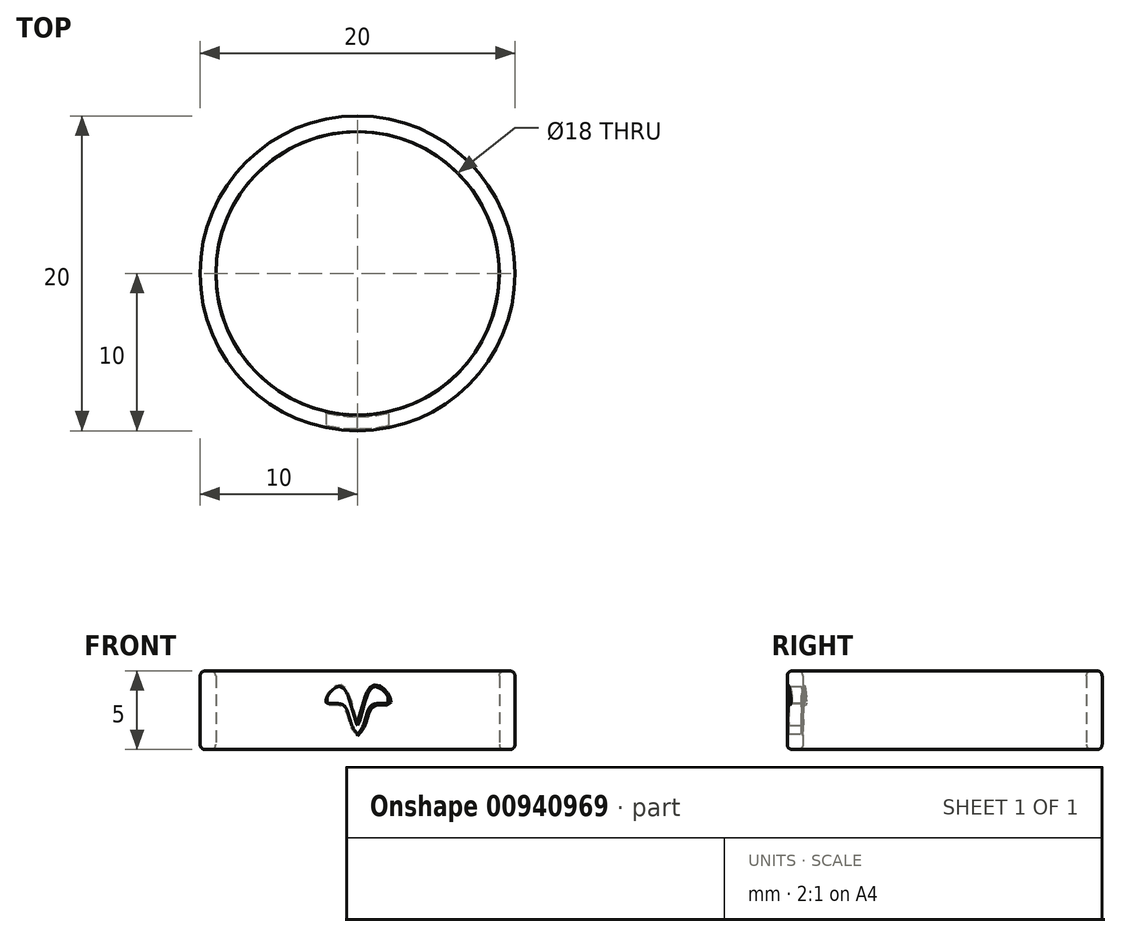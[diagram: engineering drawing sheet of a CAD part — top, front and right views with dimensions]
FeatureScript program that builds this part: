
annotation { "Feature Type Name" : "Feature", "Feature Type Description" : "" }
export const myFeature = defineFeature(function(context is Context, id is Id, definition is map)
    precondition{}
    {
        {
            var Q0;
            Q0=qCreatedBy(makeId("Front.planeOp"),FACE);
            var sketch = newSketch(context, id + "F0", { "sketchPlane" : qUnion([Q0])});
            skLineSegment(sketch, "E0", {"start": v(0, 0) * mm, "end": v(0, 2.47) * mm, "construction": true});
            skLineSegment(sketch, "E1.bottom", {"start": v(9, 0) * mm, "end": v(10, 0) * mm});
            skLineSegment(sketch, "E1.top", {"start": v(9, 5) * mm, "end": v(10, 5) * mm});
            skLineSegment(sketch, "E1.left", {"start": v(9, 0) * mm, "end": v(9, 5) * mm});
            skLineSegment(sketch, "E1.right", {"start": v(10, 0) * mm, "end": v(10, 5) * mm});
            skSolve(sketch);
        }
        {
            var Q0;
            Q0=makeQuery(id+"F0.imprint","IMPRINT",FACE,{"disambiguationData":[TD([[makeQuery(id+"F0.imprint","IMPRINT",EDGE,{"derivedFrom":sQuery(id+"F0.wireOp",EDGE,"E1.bottom")}),1.0]])]});
            var Q1;
            Q1=sQuery(id+"F0.wireOp",EDGE,"E0");
            revolve(context, id + "F1", {"surfaceOperationType" : NewSurfaceOperationType.NEW, "entities" : qUnion([Q0]), "axis" : qUnion([Q1]), "revolveType" : RevolveType.FULL});
        }
        {
            var Q0;
            Q0=makeQuery(id+"F1.opRevolve","SWEPT_EDGE",EDGE,{"disambiguationData":[OSD([sQuery(id+"F0.wireOp",EDGE,"E1.bottom"),sQuery(id+"F0.wireOp",EDGE,"E1.left")])]});
            var Q1;
            Q1=makeQuery(id+"F1.opRevolve","SWEPT_EDGE",EDGE,{"disambiguationData":[OSD([sQuery(id+"F0.wireOp",EDGE,"E1.top"),sQuery(id+"F0.wireOp",EDGE,"E1.left")])]});
            var Q2;
            Q2=makeQuery(id+"F1.opRevolve","SWEPT_EDGE",EDGE,{"disambiguationData":[OSD([sQuery(id+"F0.wireOp",EDGE,"E1.top"),sQuery(id+"F0.wireOp",EDGE,"E1.right")])]});
            var Q3;
            Q3=makeQuery(id+"F1.opRevolve","SWEPT_EDGE",EDGE,{"disambiguationData":[OSD([sQuery(id+"F0.wireOp",EDGE,"E1.bottom"),sQuery(id+"F0.wireOp",EDGE,"E1.right")])]});
            fillet(context, id + "F2", {"entities" : qUnion([Q0, Q1, Q2, Q3]), "radius" : .33 * mm, "tangentPropagation" : true, "allowEdgeOverflow" : false});
        }
        {
            var Q0;
            Q0=qCreatedBy(makeId("Front.planeOp"),FACE);
            var sketch = newSketch(context, id + "F3", { "sketchPlane" : qUnion([Q0])});
            skLineSegment(sketch, "E2", {"start": v(0, 0) * mm, "end": v(0, 7.67) * mm, "construction": true});
            skLineSegment(sketch, "E3", {"start": v(0, 4) * mm, "end": v(3.23, 4) * mm, "construction": true});
            skLineSegment(sketch, "E4", {"start": v(0, 1) * mm, "end": v(2.17, 1) * mm, "construction": true});
            skLineSegment(sketch, "E5", {"start": v(2, 5.06) * mm, "end": v(2, 0.26) * mm, "construction": true});
            skFitSpline(sketch, "E6", {"points": [v(0, 1.55) * mm, v(1.08, 4) * mm, v(2, 3.03) * mm, v(0.94, 2.85) * mm, v(0, 1) * mm], "startDerivative": vector(2.7, 3.62) * mm, "endDerivative": vector(-6.5, -5.91) * mm});
            skFitSpline(sketch, "E7.MirrorCS", {"points": [v(0, 1.55) * mm, v(-1.08, 4) * mm, v(-2, 3.03) * mm, v(-0.94, 2.85) * mm, v(0, 1) * mm], "startDerivative": vector(-2.7, 3.62) * mm, "endDerivative": vector(6.5, -5.91) * mm});
            skSolve(sketch);
        }
        {
            var Q0;
            Q0=makeQuery(id+"F3.imprint","IMPRINT",FACE,{"disambiguationData":[TD([[makeQuery(id+"F3.imprint","IMPRINT",EDGE,{"derivedFrom":sQuery(id+"F3.wireOp",EDGE,"E6")}),-1.0]])]});
            extrude(context, id + "F4", {"entities" : qUnion([Q0]), "operationType" : NewBodyOperationType.REMOVE, "endBound" : BoundingType.THROUGH_ALL, "depth" : 25 * mm, "offsetDistance" : 25 * mm});
        }
        {
            var Q0;
            Q0=makeQuery(id+"F4.boolean.opBoolean","INTERSECT",EDGE,{"derivedFrom":[makeQuery(id+"F1.opRevolve","SWEPT_FACE",FACE,{"disambiguationData":[OSD([sQuery(id+"F0.wireOp",EDGE,"E1.right")])]}),makeQuery(id+"F4.opExtrude","SWEPT_FACE",FACE,{"disambiguationData":[OSD([sQuery(id+"F3.wireOp",EDGE,"E6")])]})]});
            var Q1;
            Q1=makeQuery(id+"F4.boolean.opBoolean","INTERSECT",EDGE,{"derivedFrom":[makeQuery(id+"F1.opRevolve","SWEPT_FACE",FACE,{"disambiguationData":[OSD([sQuery(id+"F0.wireOp",EDGE,"E1.right")])]}),makeQuery(id+"F4.opExtrude","SWEPT_FACE",FACE,{"disambiguationData":[OSD([sQuery(id+"F3.wireOp",EDGE,"E7.MirrorCS")])]})]});
            var Q2;
            Q2=makeQuery(id+"F4.boolean.opBoolean","INTERSECT",EDGE,{"derivedFrom":[makeQuery(id+"F1.opRevolve","SWEPT_FACE",FACE,{"disambiguationData":[OSD([sQuery(id+"F0.wireOp",EDGE,"E1.left")])]}),makeQuery(id+"F4.opExtrude","SWEPT_FACE",FACE,{"disambiguationData":[OSD([sQuery(id+"F3.wireOp",EDGE,"E7.MirrorCS")])]})]});
            var Q3;
            Q3=makeQuery(id+"F4.boolean.opBoolean","INTERSECT",EDGE,{"derivedFrom":[makeQuery(id+"F1.opRevolve","SWEPT_FACE",FACE,{"disambiguationData":[OSD([sQuery(id+"F0.wireOp",EDGE,"E1.left")])]}),makeQuery(id+"F4.opExtrude","SWEPT_FACE",FACE,{"disambiguationData":[OSD([sQuery(id+"F3.wireOp",EDGE,"E6")])]})]});
            fillet(context, id + "F5", {"entities" : qUnion([Q0, Q1, Q2, Q3]), "radius" : .1 * mm, "tangentPropagation" : true, "allowEdgeOverflow" : false});
        }
    });
